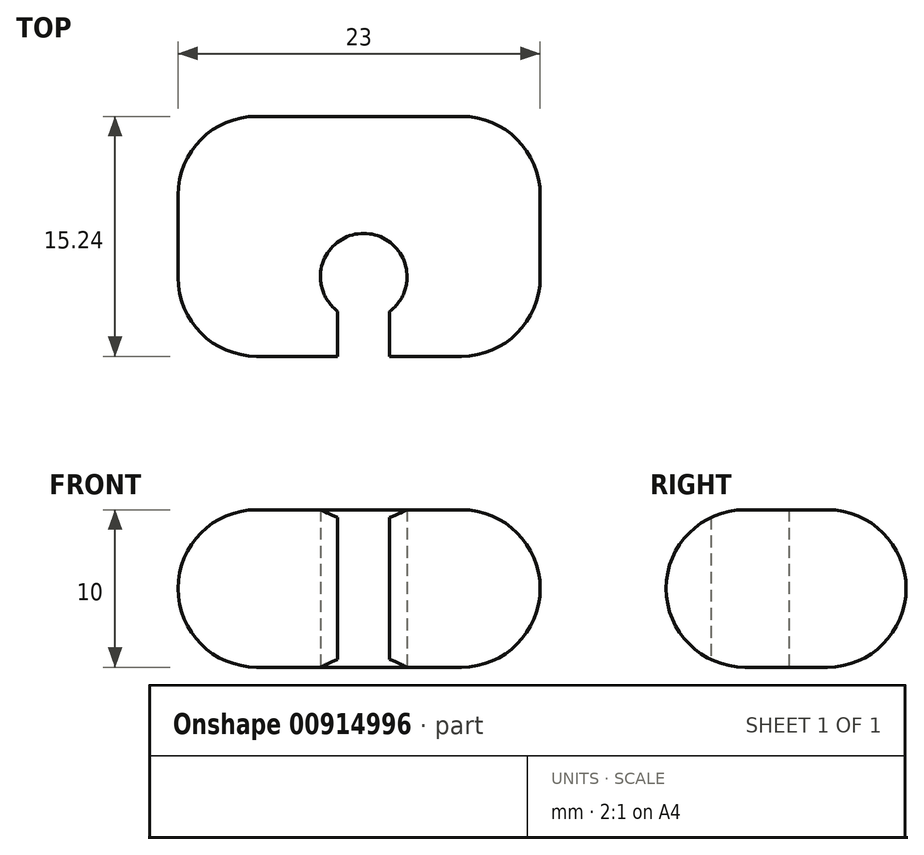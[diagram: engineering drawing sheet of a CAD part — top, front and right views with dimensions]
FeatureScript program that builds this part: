
annotation { "Feature Type Name" : "Feature", "Feature Type Description" : "" }
export const myFeature = defineFeature(function(context is Context, id is Id, definition is map)
    precondition{}
    {
        {
            var Q0;
            Q0=qCreatedBy(makeId("Top.planeOp"),FACE);
            var sketch = newSketch(context, id + "F0", { "sketchPlane" : qUnion([Q0])});
            skLineSegment(sketch, "E0", {"start": v(0, 0) * mm, "end": v(-11.8, 0) * mm});
            skLineSegment(sketch, "E1", {"start": v(0, 0) * mm, "end": v(11.2, 0) * mm});
            skLineSegment(sketch, "E2", {"start": v(-11.8, 0) * mm, "end": v(-11.8, 15.24) * mm});
            skLineSegment(sketch, "E3", {"start": v(-11.8, 15.24) * mm, "end": v(11.2, 15.24) * mm});
            skLineSegment(sketch, "E4", {"start": v(11.2, 15.24) * mm, "end": v(11.2, 0) * mm});
            skCircle(sketch, "E5", {"center": v(0, 5.05) * mm, "radius": 2.75 * mm});
            skLineSegment(sketch, "E6", {"start": v(0, 0) * mm, "end": v(0, 2.3) * mm});
            skLineSegment(sketch, "E7", {"start": v(0, 2.3) * mm, "end": v(0, 0) * mm});
            skPoint(sketch, "E8", {"position": v(0, 2.3) * mm});
            skLineSegment(sketch, "E9", {"start": v(0, 2.3) * mm, "end": v(0, 0) * mm, "construction": true});
            skPoint(sketch, "E10", {"position": v(-1.65, 2.85) * mm});
            skPoint(sketch, "E11", {"position": v(1.65, 2.85) * mm});
            skLineSegment(sketch, "E12", {"start": v(-1.65, 2.85) * mm, "end": v(-1.65, 0) * mm});
            skLineSegment(sketch, "E13", {"start": v(1.65, 2.85) * mm, "end": v(1.65, 0) * mm});
            skSolve(sketch);
        }
        {
            var Q0;
            {var subQ0=sQuery(id+"F0.wireOp",EDGE,"E2");Q0=makeQuery(id+"F0.imprint","IMPRINT",FACE,{"disambiguationData":[TD([[makeQuery(id+"F0.imprint","IMPRINT",EDGE,{"derivedFrom":subQ0}),-1.0]])]});}
            extrude(context, id + "F1", {"entities" : qUnion([Q0]), "depth" : 10 * mm, "offsetDistance" : 25.4 * mm});
        }
        {
            var Q0;
            Q0=makeQuery(id+"F1.opExtrude","CAP_EDGE",EDGE,{"disambiguationData":[OSD([sQuery(id+"F0.wireOp",EDGE,"E4")])],"isStart":false});
            var Q1;
            Q1=makeQuery(id+"F1.opExtrude","CAP_EDGE",EDGE,{"disambiguationData":[OSD([sQuery(id+"F0.wireOp",EDGE,"E4")])],"isStart":true});
            var Q2;
            Q2=makeQuery(id+"F1.opExtrude","CAP_EDGE",EDGE,{"disambiguationData":[OSD([sQuery(id+"F0.wireOp",EDGE,"E2")])],"isStart":true});
            var Q3;
            Q3=makeQuery(id+"F1.opExtrude","CAP_EDGE",EDGE,{"disambiguationData":[OSD([sQuery(id+"F0.wireOp",EDGE,"E2")])],"isStart":false});
            fillet(context, id + "F2", {"entities" : qUnion([Q0, Q1, Q2, Q3]), "radius" : 5 * mm, "tangentPropagation" : true, "allowEdgeOverflow" : false});
        }
        {
            var Q0;
            Q0=makeQuery(id+"F1.opExtrude","CAP_EDGE",EDGE,{"disambiguationData":[OSD([sQuery(id+"F0.wireOp",EDGE,"E3")])],"isStart":false});
            var Q1;
            Q1=makeQuery(id+"F2.opFillet","BLEND_EDGE",EDGE,{"blendedFrom":[makeQuery(id+"F1.opExtrude","CAP_EDGE",EDGE,{"disambiguationData":[OSD([sQuery(id+"F0.wireOp",EDGE,"E2")])],"isStart":true}),makeQuery(id+"F1.opExtrude","SWEPT_FACE",FACE,{"disambiguationData":[OSD([sQuery(id+"F0.wireOp",EDGE,"E0")])]})],"blendedInto":[makeQuery(id+"F1.opExtrude","SWEPT_FACE",FACE,{"disambiguationData":[OSD([sQuery(id+"F0.wireOp",EDGE,"E0")])]})]});
            var Q2;
            Q2=makeQuery(id+"F2.opFillet","BLEND_EDGE",EDGE,{"blendedFrom":[makeQuery(id+"F1.opExtrude","CAP_EDGE",EDGE,{"disambiguationData":[OSD([sQuery(id+"F0.wireOp",EDGE,"E4")])],"isStart":true}),makeQuery(id+"F1.opExtrude","SWEPT_FACE",FACE,{"disambiguationData":[OSD([sQuery(id+"F0.wireOp",EDGE,"E1")])]})],"blendedInto":[makeQuery(id+"F1.opExtrude","SWEPT_FACE",FACE,{"disambiguationData":[OSD([sQuery(id+"F0.wireOp",EDGE,"E1")])]})]});
            fillet(context, id + "F3", {"entities" : qUnion([Q0, Q1, Q2]), "radius" : 5 * mm, "tangentPropagation" : true, "allowEdgeOverflow" : false});
        }
    });
